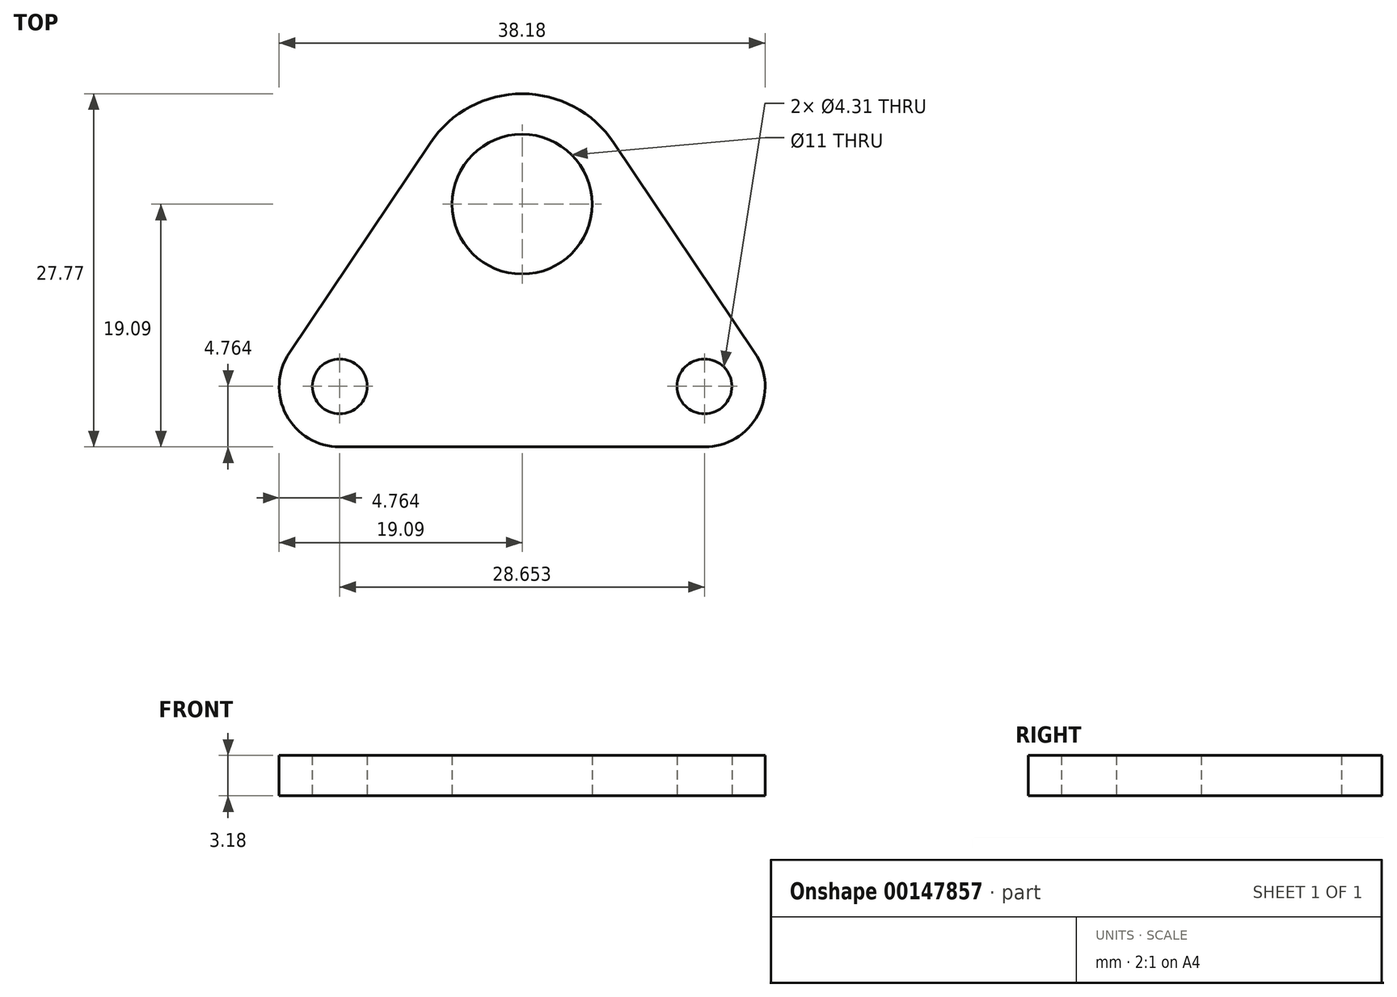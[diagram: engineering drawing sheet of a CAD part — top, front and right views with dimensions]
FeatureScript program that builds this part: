
annotation { "Feature Type Name" : "Feature", "Feature Type Description" : "" }
export const myFeature = defineFeature(function(context is Context, id is Id, definition is map)
    precondition{}
    {
        {
            var Q0;
            Q0=qCreatedBy(makeId("Top.planeOp"),FACE);
            var sketch = newSketch(context, id + "F0", { "sketchPlane" : qUnion([Q0])});
            skCircle(sketch, "E0", {"center": v(0, 0) * mm, "radius": 5.5 * mm});
            skArc(sketch, "E1", {"start": v(7.2, 4.83) * mm, "mid": v(0, 8.68) * mm, "end": v(-7.2, 4.83) * mm});
            skLineSegment(sketch, "E2", {"start": v(7.2, 4.83) * mm, "end": v(18.28, -11.67) * mm});
            skLineSegment(sketch, "E3", {"start": v(-7.2, 4.83) * mm, "end": v(-18.28, -11.67) * mm});
            skLineSegment(sketch, "E4", {"start": v(0, 0) * mm, "end": v(0, -14.33) * mm, "construction": true});
            skLineSegment(sketch, "E5", {"start": v(-14.33, -14.33) * mm, "end": v(14.33, -14.33) * mm, "construction": true});
            skLineSegment(sketch, "E6", {"start": v(-14.33, -19.09) * mm, "end": v(14.33, -19.09) * mm});
            skArc(sketch, "E7", {"start": v(-18.28, -11.67) * mm, "mid": v(-18.53, -16.57) * mm, "end": v(-14.33, -19.09) * mm});
            skArc(sketch, "E8", {"start": v(14.33, -19.09) * mm, "mid": v(18.53, -16.57) * mm, "end": v(18.28, -11.67) * mm});
            skCircle(sketch, "E9", {"center": v(-14.33, -14.33) * mm, "radius": 2.15 * mm});
            skCircle(sketch, "E10", {"center": v(14.33, -14.33) * mm, "radius": 2.15 * mm});
            skArc(sketch, "E11", {"start": v(18.28, -11.67) * mm, "mid": v(10.12, -12.09) * mm, "end": v(14.33, -19.09) * mm, "construction": true});
            skCircle(sketch, "E12", {"center": v(0, 0) * mm, "radius": 15.5 * mm, "construction": true});
            skLineSegment(sketch, "E13", {"start": v(0, 0) * mm, "end": v(14.33, -14.33) * mm, "construction": true});
            skSolve(sketch);
        }
        {
            var Q0;
            Q0=qSketchRegion(id+"F0",true);
            extrude(context, id + "F1", {"entities" : qUnion([Q0]), "depth" : 3.17 * mm});
        }
    });
